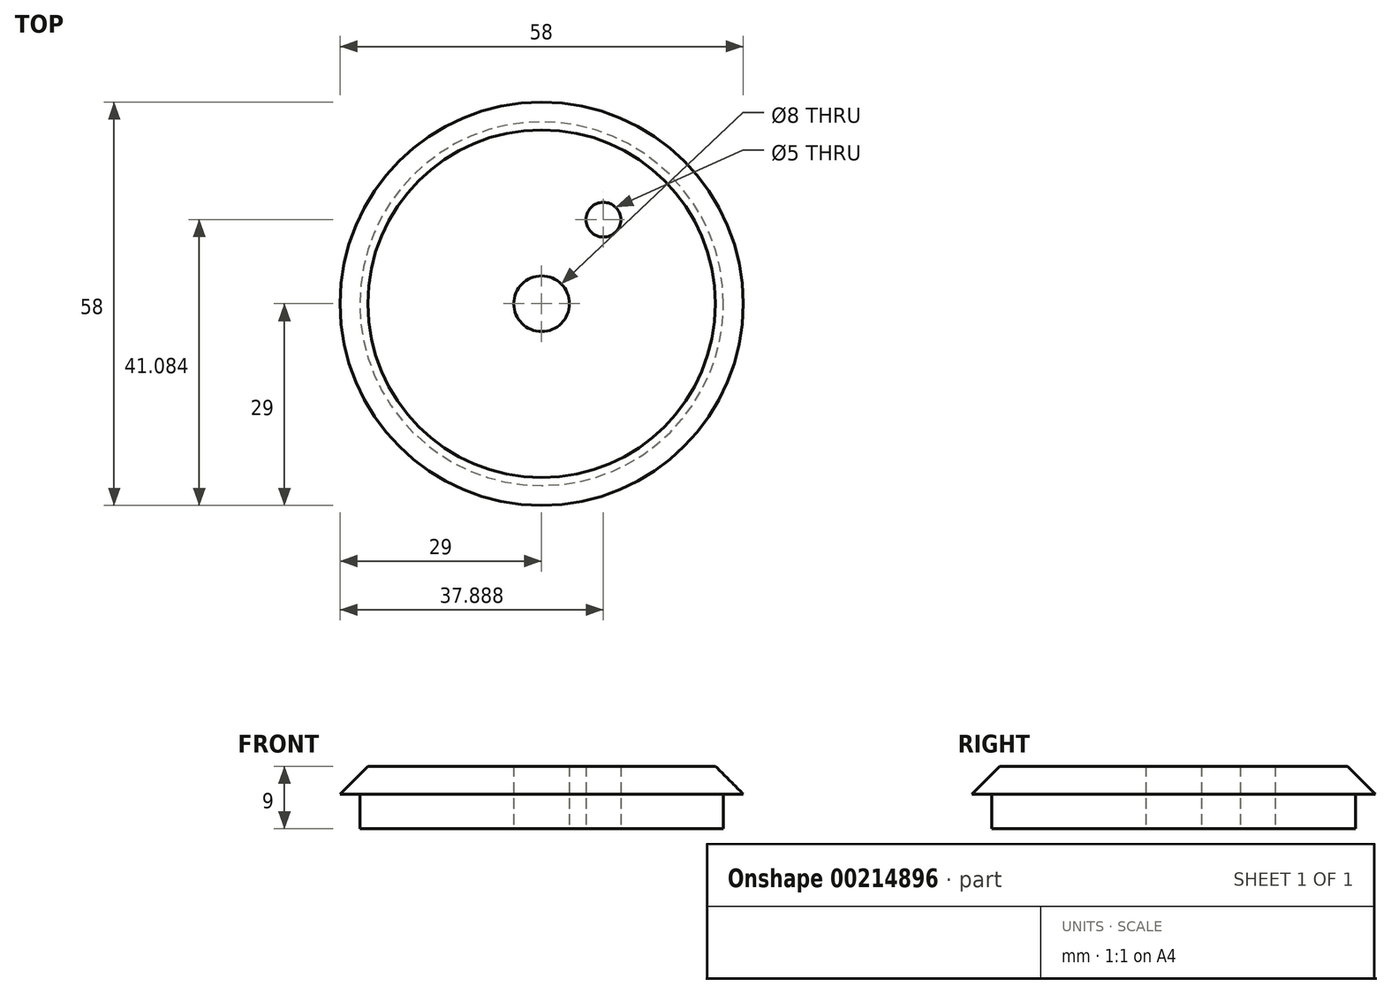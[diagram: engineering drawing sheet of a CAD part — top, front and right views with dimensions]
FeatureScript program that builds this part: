
annotation { "Feature Type Name" : "Feature", "Feature Type Description" : "" }
export const myFeature = defineFeature(function(context is Context, id is Id, definition is map)
    precondition{}
    {
        {
            var Q0;
            Q0=qCreatedBy(makeId("Top.planeOp"),FACE);
            var sketch = newSketch(context, id + "F0", { "sketchPlane" : qUnion([Q0])});
            skCircle(sketch, "E0", {"center": v(0, 0) * mm, "radius": 29 * mm});
            skSolve(sketch);
        }
        {
            var Q0;
            Q0=makeQuery(id+"F0.imprint","IMPRINT",FACE,{"disambiguationData":[TD([[makeQuery(id+"F0.imprint","IMPRINT",EDGE,{"derivedFrom":sQuery(id+"F0.wireOp",EDGE,"E0")}),1.0]])]});
            extrude(context, id + "F1", {"entities" : qUnion([Q0]), "depth" : 4 * mm});
        }
        {
            var Q0;
            Q0=qCreatedBy(makeId("Top.planeOp"),FACE);
            var sketch = newSketch(context, id + "F2", { "sketchPlane" : qUnion([Q0])});
            skCircle(sketch, "E1", {"center": v(0, 0) * mm, "radius": 26.15 * mm});
            skSolve(sketch);
        }
        {
            var Q0;
            Q0=makeQuery(id+"F2.imprint","IMPRINT",FACE,{"disambiguationData":[TD([[makeQuery(id+"F2.imprint","IMPRINT",EDGE,{"derivedFrom":sQuery(id+"F2.wireOp",EDGE,"E1")}),1.0]])]});
            extrude(context, id + "F3", {"entities" : qUnion([Q0]), "operationType" : NewBodyOperationType.ADD, "oppositeDirection" : true, "depth" : 5 * mm});
        }
        {
            var Q0;
            Q0=makeQuery(id+"F1.opExtrude","CAP_EDGE",EDGE,{"disambiguationData":[OSD([sQuery(id+"F0.wireOp",EDGE,"E0")])],"isStart":false});
            chamfer(context, id + "F4", {"entities" : qUnion([Q0]), "width" : 4 * mm, "tangentPropagation" : true});
        }
        {
            var Q0;
            Q0=qCreatedBy(makeId("Top.planeOp"),FACE);
            var sketch = newSketch(context, id + "F5", { "sketchPlane" : qUnion([Q0])});
            skCircle(sketch, "E2", {"center": v(0, 0) * mm, "radius": 4 * mm});
            skSolve(sketch);
        }
        {
            var Q0;
            Q0 = qSketchRegion(id + "F5", true);
            extrude(context, id + "F6", {"entities" : qUnion([Q0]), "operationType" : NewBodyOperationType.REMOVE, "depth" : 25 * mm, "hasSecondDirection" : true, "secondDirectionOppositeDirection" : true, "secondDirectionDepth" : 25 * mm});
        }
        {
            var Q0;
            Q0=qCreatedBy(makeId("Top.planeOp"),FACE);
            var sketch = newSketch(context, id + "F7", { "sketchPlane" : qUnion([Q0])});
            skCircle(sketch, "E3", {"center": v(8.89, 12.08) * mm, "radius": 2.5 * mm});
            skSolve(sketch);
        }
        {
            var Q0;
            Q0 = qSketchRegion(id + "F7", true);
            extrude(context, id + "F8", {"entities" : qUnion([Q0]), "operationType" : NewBodyOperationType.REMOVE, "depth" : 25 * mm, "hasSecondDirection" : true, "secondDirectionOppositeDirection" : true, "secondDirectionDepth" : 25 * mm});
        }
    });
